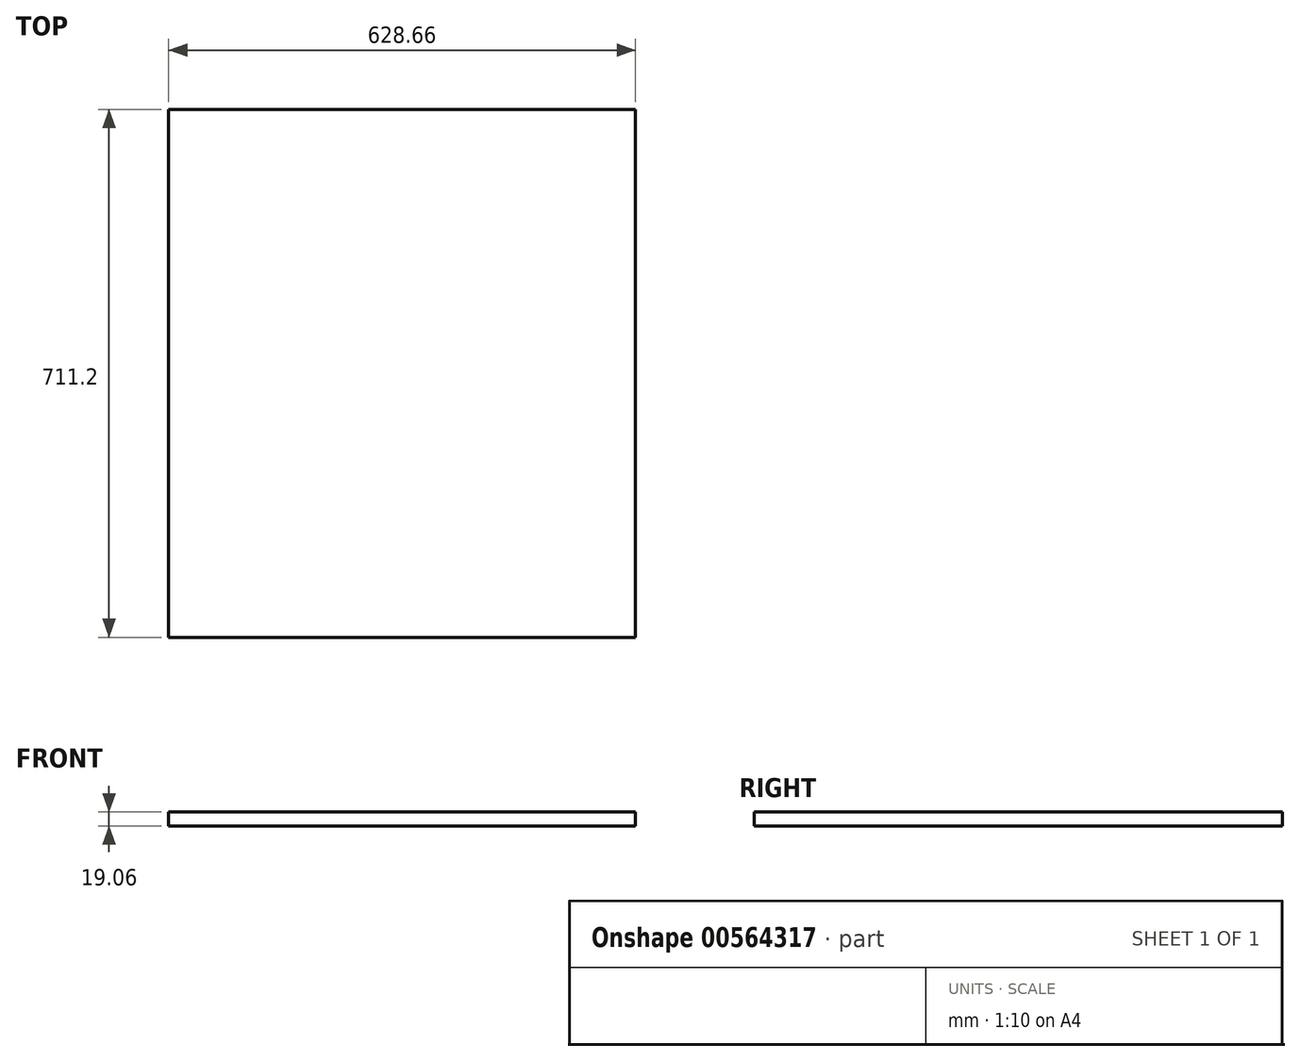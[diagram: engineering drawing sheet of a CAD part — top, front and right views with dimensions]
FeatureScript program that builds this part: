
annotation { "Feature Type Name" : "Feature", "Feature Type Description" : "" }
export const myFeature = defineFeature(function(context is Context, id is Id, definition is map)
    precondition{}
    {
        {
            var Q0;
            Q0=qCreatedBy(makeId("Front.planeOp"),FACE);
            var sketch = newSketch(context, id + "F0", { "sketchPlane" : qUnion([Q0])});
            skLineSegment(sketch, "E0.bottom", {"start": v(-314.32, 9.53) * mm, "end": v(314.33, 9.53) * mm});
            skLineSegment(sketch, "E0.top", {"start": v(-314.32, -9.53) * mm, "end": v(314.33, -9.53) * mm});
            skLineSegment(sketch, "E0.left", {"start": v(-314.33, 9.53) * mm, "end": v(-314.33, -9.53) * mm});
            skLineSegment(sketch, "E0.right", {"start": v(314.33, 9.53) * mm, "end": v(314.33, -9.53) * mm});
            skPoint(sketch, "E0.middle", {"position": v(0, 0) * mm});
            skSolve(sketch);
        }
        {
            var Q0;
            Q0=makeQuery(id+"F0.imprint","IMPRINT",FACE,{"disambiguationData":[TD([[makeQuery(id+"F0.imprint","IMPRINT",EDGE,{"derivedFrom":sQuery(id+"F0.wireOp",EDGE,"E0.bottom")}),-1.0]])]});
            extrude(context, id + "F1", {"entities" : qUnion([Q0]), "depth" : 711.2 * mm, "offsetDistance" : 25.4 * mm});
        }
    });
